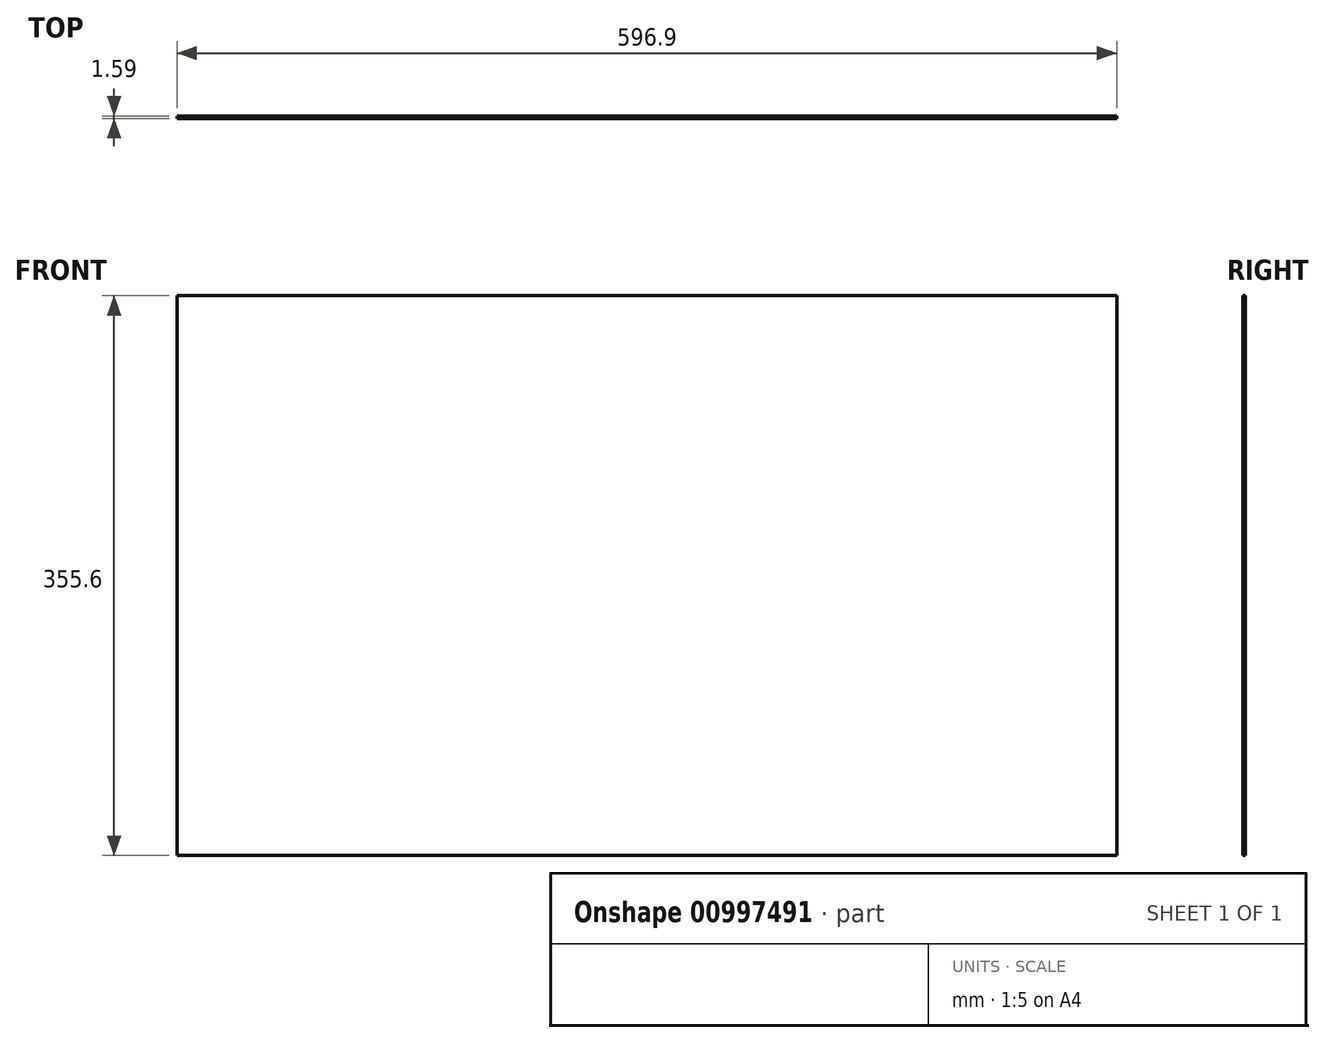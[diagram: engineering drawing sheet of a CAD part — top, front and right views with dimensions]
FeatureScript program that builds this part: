
annotation { "Feature Type Name" : "Feature", "Feature Type Description" : "" }
export const myFeature = defineFeature(function(context is Context, id is Id, definition is map)
    precondition{}
    {
        {
            var Q0;
            Q0=qCreatedBy(makeId("Front.planeOp"),FACE);
            var sketch = newSketch(context, id + "F0", { "sketchPlane" : qUnion([Q0])});
            skLineSegment(sketch, "E0.bottom", {"start": v(0, 0) * mm, "end": v(596.9, 0) * mm});
            skLineSegment(sketch, "E0.top", {"start": v(0, 355.6) * mm, "end": v(596.9, 355.6) * mm});
            skLineSegment(sketch, "E0.left", {"start": v(0, 0) * mm, "end": v(0, 355.6) * mm});
            skLineSegment(sketch, "E0.right", {"start": v(596.9, 0) * mm, "end": v(596.9, 355.6) * mm});
            skSolve(sketch);
        }
        {
            var Q0;
            Q0 = qSketchRegion(id + "F0", true);
            extrude(context, id + "F1", {"entities" : qUnion([Q0]), "depth" : 1.59 * mm, "offsetDistance" : 25.4 * mm});
        }
    });
